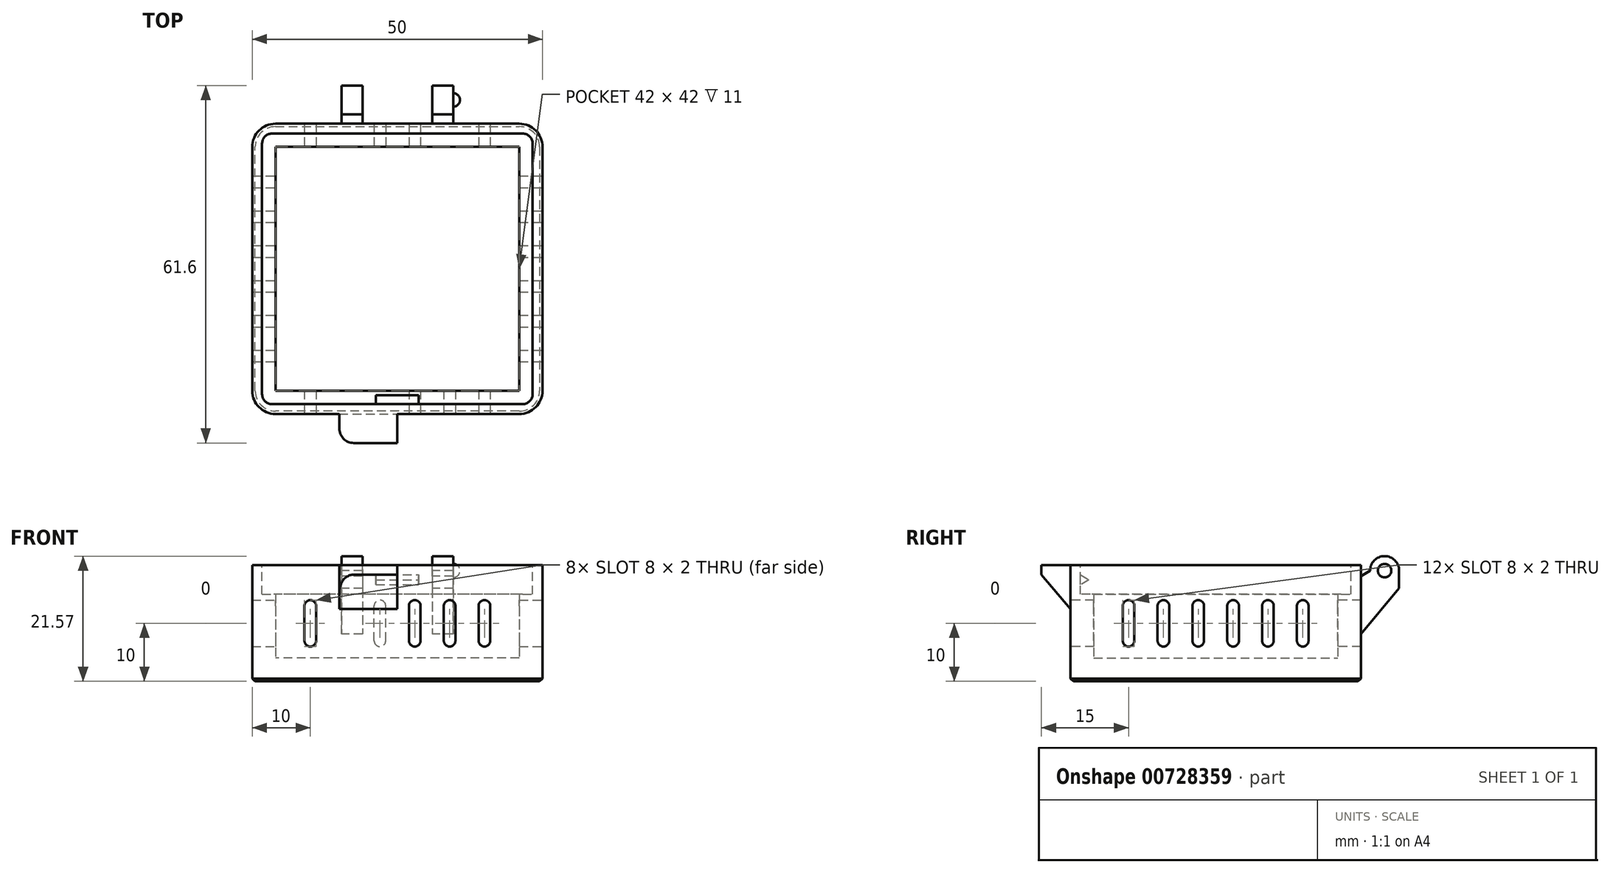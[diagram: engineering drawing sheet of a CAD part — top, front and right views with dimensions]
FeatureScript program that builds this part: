
annotation { "Feature Type Name" : "Feature", "Feature Type Description" : "" }
export const myFeature = defineFeature(function(context is Context, id is Id, definition is map)
    precondition{}
    {
        {
            var Q0;
            Q0=qCreatedBy(makeId("Top.planeOp"),FACE);
            var sketch = newSketch(context, id + "F0", { "sketchPlane" : qUnion([Q0])});
            skLineSegment(sketch, "E0.bottom", {"start": v(25, -25) * mm, "end": v(-25, -25) * mm});
            skLineSegment(sketch, "E0.top", {"start": v(25, 25) * mm, "end": v(-25, 25) * mm});
            skLineSegment(sketch, "E0.left", {"start": v(25, -25) * mm, "end": v(25, 25) * mm});
            skLineSegment(sketch, "E0.right", {"start": v(-25, -25) * mm, "end": v(-25, 25) * mm});
            skPoint(sketch, "E0.middle", {"position": v(0, 0) * mm});
            skSolve(sketch);
        }
        {
            var Q0;
            Q0=qSketchRegion(id+"F0",true);
            extrude(context, id + "F1", {"entities" : qUnion([Q0]), "depth" : 20 * mm, "offsetDistance" : 25 * mm});
        }
        {
            var Q0;
            Q0=makeQuery(id+"F1.opExtrude","CAP_FACE",FACE,{"disambiguationData":[OSD([sQuery(id+"F0.wireOp",EDGE,"E0.bottom"),sQuery(id+"F0.wireOp",EDGE,"E0.top"),sQuery(id+"F0.wireOp",EDGE,"E0.left"),sQuery(id+"F0.wireOp",EDGE,"E0.right")])],"isStart":false});
            shell(context, id + "F2", {"entities" : qUnion([Q0]), "thickness" : 4 * mm});
        }
        {
            var Q0;
            Q0=makeQuery(id+"F1.opExtrude","SWEPT_EDGE",EDGE,{"disambiguationData":[OSD([sQuery(id+"F0.wireOp",EDGE,"E0.bottom"),sQuery(id+"F0.wireOp",EDGE,"E0.right")])]});
            var Q1;
            Q1=makeQuery(id+"F1.opExtrude","SWEPT_EDGE",EDGE,{"disambiguationData":[OSD([sQuery(id+"F0.wireOp",EDGE,"E0.bottom"),sQuery(id+"F0.wireOp",EDGE,"E0.left")])]});
            var Q2;
            Q2=makeQuery(id+"F1.opExtrude","SWEPT_EDGE",EDGE,{"disambiguationData":[OSD([sQuery(id+"F0.wireOp",EDGE,"E0.top"),sQuery(id+"F0.wireOp",EDGE,"E0.left")])]});
            var Q3;
            Q3=makeQuery(id+"F1.opExtrude","SWEPT_EDGE",EDGE,{"disambiguationData":[OSD([sQuery(id+"F0.wireOp",EDGE,"E0.top"),sQuery(id+"F0.wireOp",EDGE,"E0.right")])]});
            fillet(context, id + "F3", {"entities" : qUnion([Q0, Q1, Q2, Q3]), "radius" : 4 * mm, "tangentPropagation" : true, "allowEdgeOverflow" : false});
        }
        {
            var Q0;
            Q0=makeQuery(id+"F1.opExtrude","SWEPT_FACE",FACE,{"disambiguationData":[OSD([sQuery(id+"F0.wireOp",EDGE,"E0.bottom")])]});
            var sketch = newSketch(context, id + "F4", { "sketchPlane" : qUnion([Q0])});
            skLineSegment(sketch, "E1.bottom", {"start": v(-15, 6) * mm, "end": v(-15, 6) * mm});
            skLineSegment(sketch, "E1.top", {"start": v(-15, 14) * mm, "end": v(-15, 14) * mm});
            skLineSegment(sketch, "E1.left", {"start": v(-14, 7) * mm, "end": v(-14, 13) * mm});
            skLineSegment(sketch, "E1.right", {"start": v(-16, 7) * mm, "end": v(-16, 13) * mm});
            skPoint(sketch, "E1.middle", {"position": v(-15, 10) * mm});
            skLineSegment(sketch, "E2.1.0.0", {"start": v(-9, 14) * mm, "end": v(-9, 14) * mm});
            skLineSegment(sketch, "E2.1.0.1", {"start": v(-10, 7) * mm, "end": v(-10, 13) * mm});
            skLineSegment(sketch, "E2.1.0.2", {"start": v(-9, 6) * mm, "end": v(-9, 6) * mm});
            skLineSegment(sketch, "E2.1.0.3", {"start": v(-8, 7) * mm, "end": v(-8, 13) * mm});
            skPoint(sketch, "E2.1.0.4", {"position": v(-9, 10) * mm});
            skLineSegment(sketch, "E2.2.0.0", {"start": v(-3, 14) * mm, "end": v(-3, 14) * mm});
            skLineSegment(sketch, "E2.2.0.1", {"start": v(-4, 7) * mm, "end": v(-4, 13) * mm});
            skLineSegment(sketch, "E2.2.0.2", {"start": v(-3, 6) * mm, "end": v(-3, 6) * mm});
            skLineSegment(sketch, "E2.2.0.3", {"start": v(-2, 7) * mm, "end": v(-2, 13) * mm});
            skPoint(sketch, "E2.2.0.4", {"position": v(-3, 10) * mm});
            skLineSegment(sketch, "E2.3.0.0", {"start": v(3, 14) * mm, "end": v(3, 14) * mm});
            skLineSegment(sketch, "E2.3.0.1", {"start": v(2, 7) * mm, "end": v(2, 13) * mm});
            skLineSegment(sketch, "E2.3.0.2", {"start": v(3, 6) * mm, "end": v(3, 6) * mm});
            skLineSegment(sketch, "E2.3.0.3", {"start": v(4, 7) * mm, "end": v(4, 13) * mm});
            skPoint(sketch, "E2.3.0.4", {"position": v(3, 10) * mm});
            skLineSegment(sketch, "E2.4.0.0", {"start": v(9, 14) * mm, "end": v(9, 14) * mm});
            skLineSegment(sketch, "E2.4.0.1", {"start": v(8, 7) * mm, "end": v(8, 13) * mm});
            skLineSegment(sketch, "E2.4.0.2", {"start": v(9, 6) * mm, "end": v(9, 6) * mm});
            skLineSegment(sketch, "E2.4.0.3", {"start": v(10, 7) * mm, "end": v(10, 13) * mm});
            skPoint(sketch, "E2.4.0.4", {"position": v(9, 10) * mm});
            skLineSegment(sketch, "E2.direction1", {"start": v(-16, 6) * mm, "end": v(-10, 6) * mm, "construction": true});
            skLineSegment(sketch, "E3.MirrorCS", {"start": v(15, 6) * mm, "end": v(15, 6) * mm});
            skLineSegment(sketch, "E4.MirrorCS", {"start": v(16, 7) * mm, "end": v(16, 13) * mm});
            skLineSegment(sketch, "E5.MirrorCS", {"start": v(14, 7) * mm, "end": v(14, 13) * mm});
            skLineSegment(sketch, "E6.MirrorCS", {"start": v(15, 14) * mm, "end": v(15, 14) * mm});
            skPoint(sketch, "E7.MirrorP", {"position": v(15, 10) * mm});
            skLineSegment(sketch, "E8.MirrorCS", {"start": v(16, 6) * mm, "end": v(10, 6) * mm, "construction": true});
            skPoint(sketch, "E9.visualSharp", {"position": v(-16, 14) * mm});
            skArc(sketch, "E9.filletArc", {"start": v(-15, 14) * mm, "mid": v(-15.7, 13.7) * mm, "end": v(-16, 13) * mm});
            skPoint(sketch, "E10.visualSharp", {"position": v(-14, 14) * mm});
            skArc(sketch, "E10.filletArc", {"start": v(-14, 13) * mm, "mid": v(-14.3, 13.7) * mm, "end": v(-15, 14) * mm});
            skPoint(sketch, "E11.visualSharp", {"position": v(-16, 6) * mm});
            skArc(sketch, "E11.filletArc", {"start": v(-16, 7) * mm, "mid": v(-15.7, 6.3) * mm, "end": v(-15, 6) * mm});
            skPoint(sketch, "E12.visualSharp", {"position": v(-14, 6) * mm});
            skArc(sketch, "E12.filletArc", {"start": v(-15, 6) * mm, "mid": v(-14.3, 6.3) * mm, "end": v(-14, 7) * mm});
            skPoint(sketch, "E13.visualSharp", {"position": v(-10, 14) * mm});
            skArc(sketch, "E13.filletArc", {"start": v(-9, 14) * mm, "mid": v(-9.7, 13.7) * mm, "end": v(-10, 13) * mm});
            skPoint(sketch, "E14.visualSharp", {"position": v(-8, 14) * mm});
            skArc(sketch, "E14.filletArc", {"start": v(-8, 13) * mm, "mid": v(-8.3, 13.7) * mm, "end": v(-9, 14) * mm});
            skPoint(sketch, "E15.visualSharp", {"position": v(-8, 6) * mm});
            skArc(sketch, "E15.filletArc", {"start": v(-9, 6) * mm, "mid": v(-8.3, 6.3) * mm, "end": v(-8, 7) * mm});
            skPoint(sketch, "E16.visualSharp", {"position": v(-10, 6) * mm});
            skArc(sketch, "E16.filletArc", {"start": v(-10, 7) * mm, "mid": v(-9.7, 6.3) * mm, "end": v(-9, 6) * mm});
            skPoint(sketch, "E17.visualSharp", {"position": v(-4, 6) * mm});
            skArc(sketch, "E17.filletArc", {"start": v(-4, 7) * mm, "mid": v(-3.7, 6.3) * mm, "end": v(-3, 6) * mm});
            skPoint(sketch, "E18.visualSharp", {"position": v(-2, 6) * mm});
            skArc(sketch, "E18.filletArc", {"start": v(-3, 6) * mm, "mid": v(-2.3, 6.3) * mm, "end": v(-2, 7) * mm});
            skPoint(sketch, "E19.visualSharp", {"position": v(-2, 14) * mm});
            skArc(sketch, "E19.filletArc", {"start": v(-2, 13) * mm, "mid": v(-2.3, 13.7) * mm, "end": v(-3, 14) * mm});
            skPoint(sketch, "E20.visualSharp", {"position": v(-4, 14) * mm});
            skArc(sketch, "E20.filletArc", {"start": v(-3, 14) * mm, "mid": v(-3.7, 13.7) * mm, "end": v(-4, 13) * mm});
            skPoint(sketch, "E21.visualSharp", {"position": v(2, 14) * mm});
            skArc(sketch, "E21.filletArc", {"start": v(3, 14) * mm, "mid": v(2.3, 13.7) * mm, "end": v(2, 13) * mm});
            skPoint(sketch, "E22.visualSharp", {"position": v(4, 14) * mm});
            skArc(sketch, "E22.filletArc", {"start": v(4, 13) * mm, "mid": v(3.7, 13.7) * mm, "end": v(3, 14) * mm});
            skPoint(sketch, "E23.visualSharp", {"position": v(4, 6) * mm});
            skArc(sketch, "E23.filletArc", {"start": v(3, 6) * mm, "mid": v(3.7, 6.3) * mm, "end": v(4, 7) * mm});
            skPoint(sketch, "E24.visualSharp", {"position": v(2, 6) * mm});
            skArc(sketch, "E24.filletArc", {"start": v(2, 7) * mm, "mid": v(2.3, 6.3) * mm, "end": v(3, 6) * mm});
            skPoint(sketch, "E25.visualSharp", {"position": v(10, 14) * mm});
            skArc(sketch, "E25.filletArc", {"start": v(10, 13) * mm, "mid": v(9.7, 13.7) * mm, "end": v(9, 14) * mm});
            skPoint(sketch, "E26.visualSharp", {"position": v(8, 14) * mm});
            skArc(sketch, "E26.filletArc", {"start": v(9, 14) * mm, "mid": v(8.3, 13.7) * mm, "end": v(8, 13) * mm});
            skPoint(sketch, "E27.visualSharp", {"position": v(8, 6) * mm});
            skArc(sketch, "E27.filletArc", {"start": v(8, 7) * mm, "mid": v(8.3, 6.3) * mm, "end": v(9, 6) * mm});
            skPoint(sketch, "E28.visualSharp", {"position": v(10, 6) * mm});
            skArc(sketch, "E28.filletArc", {"start": v(9, 6) * mm, "mid": v(9.7, 6.3) * mm, "end": v(10, 7) * mm});
            skPoint(sketch, "E29.visualSharp", {"position": v(16, 14) * mm});
            skArc(sketch, "E29.filletArc", {"start": v(16, 13) * mm, "mid": v(15.7, 13.7) * mm, "end": v(15, 14) * mm});
            skPoint(sketch, "E30.visualSharp", {"position": v(14, 14) * mm});
            skArc(sketch, "E30.filletArc", {"start": v(15, 14) * mm, "mid": v(14.3, 13.7) * mm, "end": v(14, 13) * mm});
            skPoint(sketch, "E31.visualSharp", {"position": v(16, 6) * mm});
            skArc(sketch, "E31.filletArc", {"start": v(15, 6) * mm, "mid": v(15.7, 6.3) * mm, "end": v(16, 7) * mm});
            skPoint(sketch, "E32.visualSharp", {"position": v(14, 6) * mm});
            skArc(sketch, "E32.filletArc", {"start": v(14, 7) * mm, "mid": v(14.3, 6.3) * mm, "end": v(15, 6) * mm});
            skSolve(sketch);
        }
        {
            var Q0;
            Q0=qSketchRegion(id+"F4",true);
            extrude(context, id + "F5", {"entities" : qUnion([Q0]), "operationType" : NewBodyOperationType.REMOVE, "oppositeDirection" : true, "depth" : 50 * mm, "offsetDistance" : 25 * mm});
        }
        {
            var Q0;
            Q0=makeQuery(id+"F1.opExtrude","SWEPT_FACE",FACE,{"disambiguationData":[OSD([sQuery(id+"F0.wireOp",EDGE,"E0.left")])]});
            var sketch = newSketch(context, id + "F6", { "sketchPlane" : qUnion([Q0])});
            skLineSegment(sketch, "E33.bottom", {"start": v(-15, 6) * mm, "end": v(-15, 6) * mm});
            skLineSegment(sketch, "E33.top", {"start": v(-15, 14) * mm, "end": v(-15, 14) * mm});
            skLineSegment(sketch, "E33.left", {"start": v(-14, 7) * mm, "end": v(-14, 13) * mm});
            skLineSegment(sketch, "E33.right", {"start": v(-16, 7) * mm, "end": v(-16, 13) * mm});
            skPoint(sketch, "E33.middle", {"position": v(-15, 10) * mm});
            skPoint(sketch, "E34.visualSharp", {"position": v(-16, 14) * mm});
            skArc(sketch, "E34.filletArc", {"start": v(-15, 14) * mm, "mid": v(-15.7, 13.7) * mm, "end": v(-16, 13) * mm});
            skPoint(sketch, "E35.visualSharp", {"position": v(-14, 14) * mm});
            skArc(sketch, "E35.filletArc", {"start": v(-14, 13) * mm, "mid": v(-14.3, 13.7) * mm, "end": v(-15, 14) * mm});
            skPoint(sketch, "E36.visualSharp", {"position": v(-14, 6) * mm});
            skArc(sketch, "E36.filletArc", {"start": v(-15, 6) * mm, "mid": v(-14.3, 6.3) * mm, "end": v(-14, 7) * mm});
            skPoint(sketch, "E37.visualSharp", {"position": v(-16, 6) * mm});
            skArc(sketch, "E37.filletArc", {"start": v(-16, 7) * mm, "mid": v(-15.7, 6.3) * mm, "end": v(-15, 6) * mm});
            skPoint(sketch, "E38.1.0.0", {"position": v(-8, 6) * mm});
            skPoint(sketch, "E38.1.0.1", {"position": v(-10, 6) * mm});
            skLineSegment(sketch, "E38.1.0.2", {"start": v(-10, 7) * mm, "end": v(-10, 13) * mm});
            skLineSegment(sketch, "E38.1.0.3", {"start": v(-8, 7) * mm, "end": v(-8, 13) * mm});
            skPoint(sketch, "E38.1.0.4", {"position": v(-8, 14) * mm});
            skPoint(sketch, "E38.1.0.5", {"position": v(-10, 14) * mm});
            skPoint(sketch, "E38.1.0.6", {"position": v(-9, 10) * mm});
            skArc(sketch, "E38.1.0.7", {"start": v(-9, 6) * mm, "mid": v(-8.3, 6.3) * mm, "end": v(-8, 7) * mm});
            skArc(sketch, "E38.1.0.8", {"start": v(-8, 13) * mm, "mid": v(-8.3, 13.7) * mm, "end": v(-9, 14) * mm});
            skArc(sketch, "E38.1.0.9", {"start": v(-9, 14) * mm, "mid": v(-9.7, 13.7) * mm, "end": v(-10, 13) * mm});
            skArc(sketch, "E38.1.0.10", {"start": v(-10, 7) * mm, "mid": v(-9.7, 6.3) * mm, "end": v(-9, 6) * mm});
            skPoint(sketch, "E38.2.0.0", {"position": v(-2, 6) * mm});
            skPoint(sketch, "E38.2.0.1", {"position": v(-4, 6) * mm});
            skLineSegment(sketch, "E38.2.0.2", {"start": v(-4, 7) * mm, "end": v(-4, 13) * mm});
            skLineSegment(sketch, "E38.2.0.3", {"start": v(-2, 7) * mm, "end": v(-2, 13) * mm});
            skPoint(sketch, "E38.2.0.4", {"position": v(-2, 14) * mm});
            skPoint(sketch, "E38.2.0.5", {"position": v(-4, 14) * mm});
            skPoint(sketch, "E38.2.0.6", {"position": v(-3, 10) * mm});
            skArc(sketch, "E38.2.0.7", {"start": v(-3, 6) * mm, "mid": v(-2.3, 6.3) * mm, "end": v(-2, 7) * mm});
            skArc(sketch, "E38.2.0.8", {"start": v(-2, 13) * mm, "mid": v(-2.3, 13.7) * mm, "end": v(-3, 14) * mm});
            skArc(sketch, "E38.2.0.9", {"start": v(-3, 14) * mm, "mid": v(-3.7, 13.7) * mm, "end": v(-4, 13) * mm});
            skArc(sketch, "E38.2.0.10", {"start": v(-4, 7) * mm, "mid": v(-3.7, 6.3) * mm, "end": v(-3, 6) * mm});
            skLineSegment(sketch, "E38.direction1", {"start": v(-16, 6) * mm, "end": v(-10, 6) * mm, "construction": true});
            skArc(sketch, "E39.MirrorCS", {"start": v(10, 7) * mm, "mid": v(9.7, 6.3) * mm, "end": v(9, 6) * mm});
            skArc(sketch, "E40.MirrorCS", {"start": v(9, 14) * mm, "mid": v(9.7, 13.7) * mm, "end": v(10, 13) * mm});
            skArc(sketch, "E41.MirrorCS", {"start": v(9, 6) * mm, "mid": v(8.3, 6.3) * mm, "end": v(8, 7) * mm});
            skArc(sketch, "E42.MirrorCS", {"start": v(16, 7) * mm, "mid": v(15.7, 6.3) * mm, "end": v(15, 6) * mm});
            skArc(sketch, "E43.MirrorCS", {"start": v(15, 6) * mm, "mid": v(14.3, 6.3) * mm, "end": v(14, 7) * mm});
            skArc(sketch, "E44.MirrorCS", {"start": v(14, 13) * mm, "mid": v(14.3, 13.7) * mm, "end": v(15, 14) * mm});
            skArc(sketch, "E45.MirrorCS", {"start": v(2, 13) * mm, "mid": v(2.3, 13.7) * mm, "end": v(3, 14) * mm});
            skArc(sketch, "E46.MirrorCS", {"start": v(3, 6) * mm, "mid": v(2.3, 6.3) * mm, "end": v(2, 7) * mm});
            skArc(sketch, "E47.MirrorCS", {"start": v(4, 7) * mm, "mid": v(3.7, 6.3) * mm, "end": v(3, 6) * mm});
            skArc(sketch, "E48.MirrorCS", {"start": v(8, 13) * mm, "mid": v(8.3, 13.7) * mm, "end": v(9, 14) * mm});
            skArc(sketch, "E49.MirrorCS", {"start": v(15, 14) * mm, "mid": v(15.7, 13.7) * mm, "end": v(16, 13) * mm});
            skArc(sketch, "E50.MirrorCS", {"start": v(3, 14) * mm, "mid": v(3.7, 13.7) * mm, "end": v(4, 13) * mm});
            skPoint(sketch, "E51.MirrorP", {"position": v(9, 10) * mm});
            skLineSegment(sketch, "E52.MirrorCS", {"start": v(4, 7) * mm, "end": v(4, 13) * mm});
            skLineSegment(sketch, "E53.MirrorCS", {"start": v(16, 6) * mm, "end": v(10, 6) * mm, "construction": true});
            skPoint(sketch, "E54.MirrorP", {"position": v(14, 14) * mm});
            skLineSegment(sketch, "E55.MirrorCS", {"start": v(8, 7) * mm, "end": v(8, 13) * mm});
            skPoint(sketch, "E56.MirrorP", {"position": v(4, 6) * mm});
            skPoint(sketch, "E57.MirrorP", {"position": v(14, 6) * mm});
            skPoint(sketch, "E58.MirrorP", {"position": v(4, 14) * mm});
            skLineSegment(sketch, "E59.MirrorCS", {"start": v(10, 7) * mm, "end": v(10, 13) * mm});
            skPoint(sketch, "E60.MirrorP", {"position": v(10, 6) * mm});
            skLineSegment(sketch, "E61.MirrorCS", {"start": v(15, 14) * mm, "end": v(15, 14) * mm});
            skLineSegment(sketch, "E62.MirrorCS", {"start": v(16, 7) * mm, "end": v(16, 13) * mm});
            skLineSegment(sketch, "E63.MirrorCS", {"start": v(14, 7) * mm, "end": v(14, 13) * mm});
            skLineSegment(sketch, "E64.MirrorCS", {"start": v(2, 7) * mm, "end": v(2, 13) * mm});
            skPoint(sketch, "E65.MirrorP", {"position": v(16, 14) * mm});
            skPoint(sketch, "E66.MirrorP", {"position": v(8, 14) * mm});
            skPoint(sketch, "E67.MirrorP", {"position": v(16, 6) * mm});
            skPoint(sketch, "E68.MirrorP", {"position": v(2, 14) * mm});
            skPoint(sketch, "E69.MirrorP", {"position": v(2, 6) * mm});
            skPoint(sketch, "E70.MirrorP", {"position": v(3, 10) * mm});
            skLineSegment(sketch, "E71.MirrorCS", {"start": v(15, 6) * mm, "end": v(15, 6) * mm});
            skPoint(sketch, "E72.MirrorP", {"position": v(15, 10) * mm});
            skPoint(sketch, "E73.MirrorP", {"position": v(8, 6) * mm});
            skPoint(sketch, "E74.MirrorP", {"position": v(10, 14) * mm});
            skSolve(sketch);
        }
        {
            var Q0;
            Q0=qSketchRegion(id+"F6",true);
            extrude(context, id + "F7", {"entities" : qUnion([Q0]), "operationType" : NewBodyOperationType.REMOVE, "endBound" : BoundingType.THROUGH_ALL, "oppositeDirection" : true, "depth" : 25 * mm, "offsetDistance" : 25 * mm});
        }
        {
            var Q0;
            Q0=makeQuery(id+"F1.opExtrude","CAP_FACE",FACE,{"disambiguationData":[OSD([sQuery(id+"F0.wireOp",EDGE,"E0.bottom"),sQuery(id+"F0.wireOp",EDGE,"E0.top"),sQuery(id+"F0.wireOp",EDGE,"E0.left"),sQuery(id+"F0.wireOp",EDGE,"E0.right")])],"isStart":false});
            var sketch = newSketch(context, id + "F8", { "sketchPlane" : qUnion([Q0])});
            skLineSegment(sketch, "E75.bottom", {"start": v(23.3, 23.3) * mm, "end": v(-23.3, 23.3) * mm});
            skLineSegment(sketch, "E75.top", {"start": v(23.3, -23.3) * mm, "end": v(-23.3, -23.3) * mm});
            skLineSegment(sketch, "E75.left", {"start": v(23.3, 23.3) * mm, "end": v(23.3, -23.3) * mm});
            skLineSegment(sketch, "E75.right", {"start": v(-23.3, 23.3) * mm, "end": v(-23.3, -23.3) * mm});
            skPoint(sketch, "E75.middle", {"position": v(0, 0) * mm});
            skSolve(sketch);
        }
        {
            var Q0;
            Q0=qSketchRegion(id+"F8",true);
            extrude(context, id + "F9", {"entities" : qUnion([Q0]), "operationType" : NewBodyOperationType.REMOVE, "oppositeDirection" : true, "depth" : 5 * mm, "offsetDistance" : 25 * mm});
        }
        {
            var Q0;
            Q0=makeQuery(id+"F9.boolean.opBoolean","COPY",EDGE,{"derivedFrom":makeQuery(id+"F9.opExtrude","SWEPT_EDGE",EDGE,{"disambiguationData":[OSD([sQuery(id+"F8.wireOp",EDGE,"E75.bottom"),sQuery(id+"F8.wireOp",EDGE,"E75.right")])]})});
            var Q1;
            Q1=makeQuery(id+"F9.boolean.opBoolean","COPY",EDGE,{"derivedFrom":makeQuery(id+"F9.opExtrude","SWEPT_EDGE",EDGE,{"disambiguationData":[OSD([sQuery(id+"F8.wireOp",EDGE,"E75.bottom"),sQuery(id+"F8.wireOp",EDGE,"E75.left")])]})});
            var Q2;
            Q2=makeQuery(id+"F9.boolean.opBoolean","COPY",EDGE,{"derivedFrom":makeQuery(id+"F9.opExtrude","SWEPT_EDGE",EDGE,{"disambiguationData":[OSD([sQuery(id+"F8.wireOp",EDGE,"E75.top"),sQuery(id+"F8.wireOp",EDGE,"E75.left")])]})});
            var Q3;
            Q3=makeQuery(id+"F9.boolean.opBoolean","COPY",EDGE,{"derivedFrom":makeQuery(id+"F9.opExtrude","SWEPT_EDGE",EDGE,{"disambiguationData":[OSD([sQuery(id+"F8.wireOp",EDGE,"E75.top"),sQuery(id+"F8.wireOp",EDGE,"E75.right")])]})});
            fillet(context, id + "F10", {"entities" : qUnion([Q0, Q1, Q2, Q3]), "radius" : 1.7 * mm, "tangentPropagation" : true, "allowEdgeOverflow" : false});
        }
        {
            var Q0;
            Q0=qCreatedBy(makeId("Right.planeOp"),FACE);
            var sketch = newSketch(context, id + "F11", { "sketchPlane" : qUnion([Q0])});
            skLineSegment(sketch, "E76", {"start": v(23.3, 18.37) * mm, "end": v(21.8, 17.5) * mm, "construction": true});
            skLineSegment(sketch, "E77", {"start": v(21.8, 17.5) * mm, "end": v(23.3, 16.63) * mm, "construction": true});
            skLineSegment(sketch, "E78", {"start": v(23.3, 16.63) * mm, "end": v(23.3, 18.37) * mm, "construction": true});
            skLineSegment(sketch, "E79.MirrorCS", {"start": v(-23.3, 18.37) * mm, "end": v(-21.8, 17.5) * mm});
            skLineSegment(sketch, "E80.MirrorCS", {"start": v(-21.8, 17.5) * mm, "end": v(-23.3, 16.63) * mm});
            skLineSegment(sketch, "E81.MirrorCS", {"start": v(-23.3, 16.63) * mm, "end": v(-23.3, 18.37) * mm});
            skSolve(sketch);
        }
        {
            var Q0;
            Q0=qSketchRegion(id+"F11",true);
            extrude(context, id + "F12", {"entities" : qUnion([Q0]), "operationType" : NewBodyOperationType.ADD, "endBound" : BoundingType.SYMMETRIC, "oppositeDirection" : true, "depth" : 7.35 * mm, "offsetDistance" : 25 * mm});
        }
        {
            var Q0;
            Q0=qCreatedBy(makeId("Right.planeOp"),FACE);
            var sketch = newSketch(context, id + "F13", { "sketchPlane" : qUnion([Q0])});
            skLineSegment(sketch, "E82", {"start": v(25, 18.15) * mm, "end": v(25, 8.15) * mm});
            skLineSegment(sketch, "E83", {"start": v(25, 8.15) * mm, "end": v(31.6, 16.02) * mm});
            skLineSegment(sketch, "E84", {"start": v(31.6, 16.02) * mm, "end": v(31.6, 21.57) * mm});
            skLineSegment(sketch, "E85", {"start": v(31.6, 21.57) * mm, "end": v(26.6, 21.57) * mm});
            skLineSegment(sketch, "E86", {"start": v(26.6, 21.57) * mm, "end": v(26.6, 19.07) * mm});
            skLineSegment(sketch, "E87", {"start": v(26.6, 19.07) * mm, "end": v(25, 18.15) * mm});
            skSolve(sketch);
        }
        {
            var Q0;
            Q0=qSketchRegion(id+"F13",true);
            extrude(context, id + "F14", {"entities" : qUnion([Q0]), "operationType" : NewBodyOperationType.ADD, "endBound" : BoundingType.SYMMETRIC, "depth" : 19.25 * mm, "offsetDistance" : 25 * mm});
        }
        {
            var Q0;
            Q0=makeQuery(id+"F14.opExtrude","SWEPT_EDGE",EDGE,{"disambiguationData":[OSD([sQuery(id+"F13.wireOp",EDGE,"E85"),sQuery(id+"F13.wireOp",EDGE,"E86")])]});
            var Q1;
            Q1=makeQuery(id+"F14.opExtrude","SWEPT_EDGE",EDGE,{"disambiguationData":[OSD([sQuery(id+"F13.wireOp",EDGE,"E84"),sQuery(id+"F13.wireOp",EDGE,"E85")])]});
            fillet(context, id + "F15", {"entities" : qUnion([Q0, Q1]), "radius" : 2.5 * mm, "tangentPropagation" : true, "allowEdgeOverflow" : false});
        }
        {
            var Q0;
            Q0=makeQuery(id+"F14.opExtrude","CAP_FACE",FACE,{"disambiguationData":[OSD([sQuery(id+"F13.wireOp",EDGE,"E82"),sQuery(id+"F13.wireOp",EDGE,"E83"),sQuery(id+"F13.wireOp",EDGE,"E84"),sQuery(id+"F13.wireOp",EDGE,"E85"),sQuery(id+"F13.wireOp",EDGE,"E86"),sQuery(id+"F13.wireOp",EDGE,"E87")])],"isStart":false});
            var sketch = newSketch(context, id + "F16", { "sketchPlane" : qUnion([Q0])});
            skArc(sketch, "E88", {"start": v(29.1, 20.23) * mm, "mid": v(30.26, 19.07) * mm, "end": v(29.1, 17.91) * mm});
            skLineSegment(sketch, "E89", {"start": v(29.1, 20.23) * mm, "end": v(29.1, 17.91) * mm});
            skSolve(sketch);
        }
        {
            var Q0;
            Q0=qSketchRegion(id+"F16",true);
            var Q1;
            Q1=sQuery(id+"F16.wireOp",EDGE,"E89");
            revolve(context, id + "F17", {"operationType" : NewBodyOperationType.ADD, "surfaceOperationType" : NewSurfaceOperationType.NEW, "entities" : qUnion([Q0]), "axis" : qUnion([Q1]), "revolveType" : RevolveType.FULL});
        }
        {
            var Q0;
            Q0=qCreatedBy(makeId("Top.planeOp"),FACE);
            var sketch = newSketch(context, id + "F18", { "sketchPlane" : qUnion([Q0])});
            skLineSegment(sketch, "E90.bottom", {"start": v(6, 25) * mm, "end": v(-6, 25) * mm});
            skLineSegment(sketch, "E90.top", {"start": v(6, 35) * mm, "end": v(-6, 35) * mm});
            skLineSegment(sketch, "E90.left", {"start": v(6, 25) * mm, "end": v(6, 35) * mm});
            skLineSegment(sketch, "E90.right", {"start": v(-6, 25) * mm, "end": v(-6, 35) * mm});
            skPoint(sketch, "E90.middle", {"position": v(0, 30) * mm});
            skSolve(sketch);
        }
        {
            var Q0;
            Q0=qSketchRegion(id+"F18",true);
            extrude(context, id + "F19", {"entities" : qUnion([Q0]), "operationType" : NewBodyOperationType.REMOVE, "depth" : 25 * mm, "offsetDistance" : 25 * mm});
        }
        {
            var Q0;
            Q0=makeQuery(id+"F19.boolean.opBoolean","MERGE",FACE,{"derivedFrom":[makeQuery(id+"F1.opExtrude","SWEPT_FACE",FACE,{"disambiguationData":[OSD([sQuery(id+"F0.wireOp",EDGE,"E0.top")])]}),makeQuery(id+"F19.opExtrude","SWEPT_FACE",FACE,{"disambiguationData":[OSD([sQuery(id+"F18.wireOp",EDGE,"E90.bottom")])]})]});
            var sketch = newSketch(context, id + "F20", { "sketchPlane" : qUnion([Q0])});
            skLineSegment(sketch, "E91.bottom", {"start": v(-7, 15) * mm, "end": v(-11, 15) * mm});
            skLineSegment(sketch, "E91.top", {"start": v(-7, 5) * mm, "end": v(-11, 5) * mm});
            skLineSegment(sketch, "E91.left", {"start": v(-7, 15) * mm, "end": v(-7, 5) * mm});
            skLineSegment(sketch, "E91.right", {"start": v(-11, 15) * mm, "end": v(-11, 5) * mm});
            skPoint(sketch, "E91.middle", {"position": v(-9, 10) * mm});
            skPoint(sketch, "E91.cornerSnap0", {"position": v(-7, 8.15) * mm});
            skLineSegment(sketch, "E92.MirrorCS", {"start": v(7, 15) * mm, "end": v(11, 15) * mm});
            skLineSegment(sketch, "E93.MirrorCS", {"start": v(7, 5) * mm, "end": v(11, 5) * mm});
            skLineSegment(sketch, "E94.MirrorCS", {"start": v(7, 15) * mm, "end": v(7, 5) * mm});
            skLineSegment(sketch, "E95.MirrorCS", {"start": v(11, 15) * mm, "end": v(11, 5) * mm});
            skPoint(sketch, "E96.MirrorP", {"position": v(9, 10) * mm});
            skPoint(sketch, "E97.MirrorP", {"position": v(7, 8.15) * mm});
            skSolve(sketch);
        }
        {
            var Q0;
            Q0=qSketchRegion(id+"F20",true);
            extrude(context, id + "F21", {"entities" : qUnion([Q0]), "operationType" : NewBodyOperationType.ADD, "oppositeDirection" : true, "depth" : 4 * mm, "offsetDistance" : 25 * mm});
        }
        {
            var Q0;
            Q0=makeQuery(id+"F1.opExtrude","SWEPT_FACE",FACE,{"disambiguationData":[OSD([sQuery(id+"F0.wireOp",EDGE,"E0.bottom")])]});
            var sketch = newSketch(context, id + "F22", { "sketchPlane" : qUnion([Q0])});
            skLineSegment(sketch, "E98.bottom", {"start": v(0, 5) * mm, "end": v(-12, 5) * mm});
            skLineSegment(sketch, "E98.top", {"start": v(0, 15) * mm, "end": v(-12, 15) * mm});
            skLineSegment(sketch, "E98.left", {"start": v(0, 5) * mm, "end": v(0, 15) * mm});
            skLineSegment(sketch, "E98.right", {"start": v(-12, 5) * mm, "end": v(-12, 15) * mm});
            skPoint(sketch, "E98.middle", {"position": v(-6, 10) * mm});
            skSolve(sketch);
        }
        {
            var Q0;
            Q0 = qSketchRegion(id + "F22", true);
            extrude(context, id + "F23", {"entities" : qUnion([Q0]), "operationType" : NewBodyOperationType.ADD, "oppositeDirection" : true, "depth" : 4 * mm, "offsetDistance" : 25 * mm});
        }
        {
            var Q0;
            Q0=qCreatedBy(makeId("Right.planeOp"),FACE);
            var sketch = newSketch(context, id + "F24", { "sketchPlane" : qUnion([Q0])});
            skLineSegment(sketch, "E99", {"start": v(-25, 20) * mm, "end": v(-30, 20) * mm});
            skLineSegment(sketch, "E100", {"start": v(-30, 20) * mm, "end": v(-30, 18.4) * mm});
            skLineSegment(sketch, "E101", {"start": v(-30, 18.4) * mm, "end": v(-25, 12.44) * mm});
            skLineSegment(sketch, "E102", {"start": v(-25, 12.44) * mm, "end": v(-25, 20) * mm});
            skSolve(sketch);
        }
        {
            var Q0;
            Q0=qSketchRegion(id+"F24",true);
            extrude(context, id + "F25", {"entities" : qUnion([Q0]), "operationType" : NewBodyOperationType.ADD, "oppositeDirection" : true, "depth" : 10 * mm, "offsetDistance" : 25 * mm});
        }
        {
            var Q0;
            Q0=makeQuery(id+"F1.opExtrude","CAP_EDGE",EDGE,{"disambiguationData":[OSD([sQuery(id+"F0.wireOp",EDGE,"E0.left")])],"isStart":true});
            chamfer(context, id + "F26", {"entities" : qUnion([Q0]), "width" : .5 * mm, "tangentPropagation" : true});
        }
        {
            var Q0;
            Q0=makeQuery(id+"F25.opExtrude","CAP_EDGE",EDGE,{"disambiguationData":[OSD([sQuery(id+"F24.wireOp",EDGE,"E100")])],"isStart":false});
            fillet(context, id + "F27", {"entities" : qUnion([Q0]), "radius" : 2.5 * mm, "tangentPropagation" : true, "allowEdgeOverflow" : false});
        }
    });
